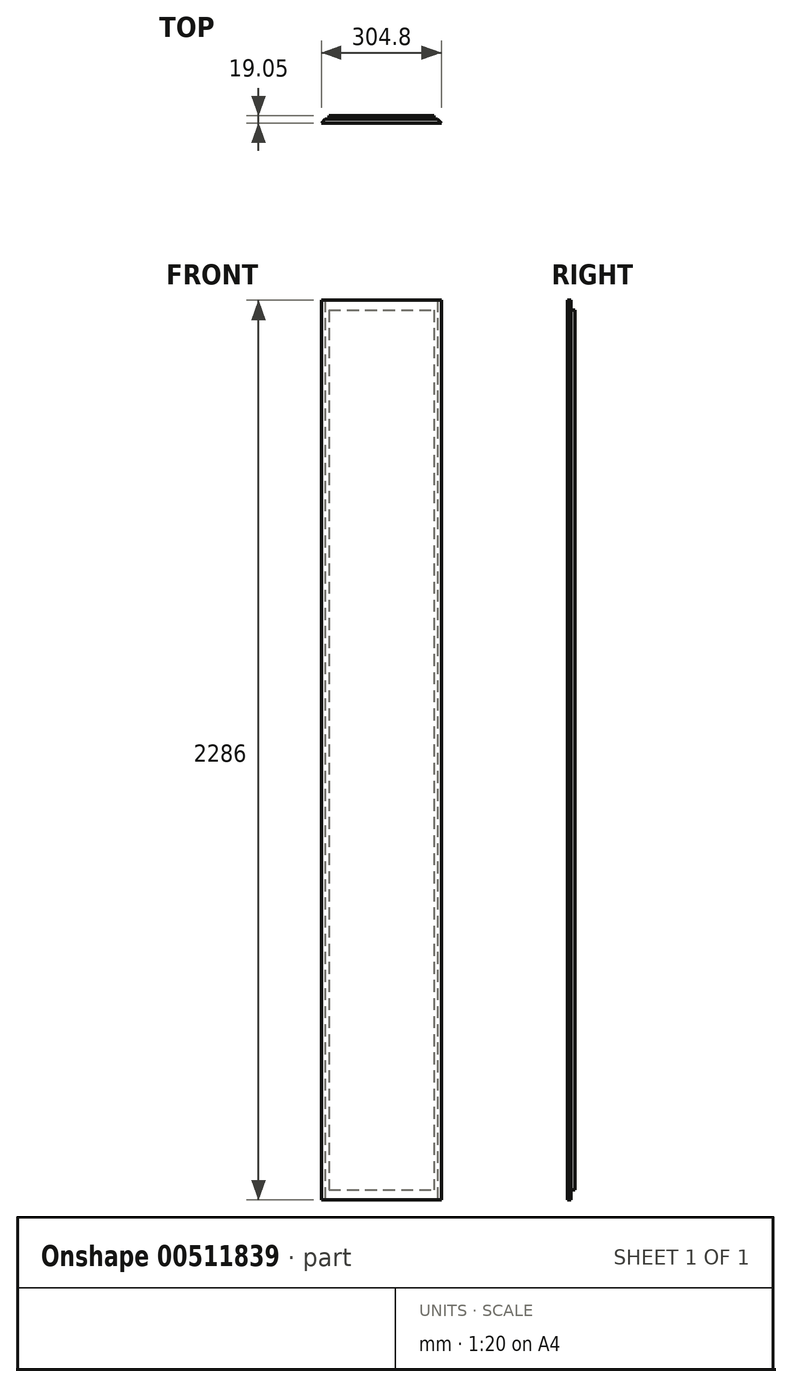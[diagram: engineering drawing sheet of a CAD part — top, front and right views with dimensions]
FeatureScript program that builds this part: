
annotation { "Feature Type Name" : "Feature", "Feature Type Description" : "" }
export const myFeature = defineFeature(function(context is Context, id is Id, definition is map)
    precondition{}
    {
        {
            var Q0;
            Q0=qCreatedBy(makeId("Top.planeOp"),FACE);
            var sketch = newSketch(context, id + "F0", { "sketchPlane" : qUnion([Q0])});
            skLineSegment(sketch, "E0.bottom", {"start": v(-140.62, 15.92) * mm, "end": v(164.18, 15.92) * mm});
            skLineSegment(sketch, "E0.top", {"start": v(-140.62, -3.13) * mm, "end": v(164.18, -3.13) * mm});
            skLineSegment(sketch, "E0.left", {"start": v(-140.62, 15.92) * mm, "end": v(-140.62, -3.13) * mm});
            skLineSegment(sketch, "E0.right", {"start": v(164.18, 15.92) * mm, "end": v(164.18, -3.13) * mm});
            skLineSegment(sketch, "E1", {"start": v(-140.62, -3.13) * mm, "end": v(-131.1, 6.4) * mm});
            skPoint(sketch, "E1.endSnap0", {"position": v(-140.62, 6.4) * mm});
            skLineSegment(sketch, "E2", {"start": v(-131.1, 6.4) * mm, "end": v(-121.57, 6.4) * mm});
            skLineSegment(sketch, "E3", {"start": v(-121.57, 6.4) * mm, "end": v(-121.57, 15.92) * mm});
            skLineSegment(sketch, "E4", {"start": v(11.78, 15.92) * mm, "end": v(11.78, -3.13) * mm, "construction": true});
            skLineSegment(sketch, "E5.MirrorCS", {"start": v(145.13, 6.4) * mm, "end": v(145.13, 15.92) * mm});
            skLineSegment(sketch, "E6.MirrorCS", {"start": v(154.66, 6.4) * mm, "end": v(145.13, 6.4) * mm});
            skLineSegment(sketch, "E7.MirrorCS", {"start": v(164.18, -3.13) * mm, "end": v(154.66, 6.4) * mm});
            skLineSegment(sketch, "E8.MirrorCS", {"start": v(164.18, 15.92) * mm, "end": v(-140.62, 15.92) * mm});
            skLineSegment(sketch, "E9", {"start": v(-121.57, 6.4) * mm, "end": v(145.13, 6.4) * mm});
            skSolve(sketch);
        }
        {
            var Q0;
            {var subQ0=sQuery(id+"F0.wireOp",EDGE,"E3");Q0=makeQuery(id+"F0.imprint","IMPRINT",FACE,{"disambiguationData":[TD([[makeQuery(id+"F0.imprint","IMPRINT",EDGE,{"derivedFrom":subQ0}),-1.0]])]});}
            var Q1;
            Q1=makeQuery(id+"F0.imprint","IMPRINT",FACE,{"disambiguationData":[TD([[makeQuery(id+"F0.imprint","IMPRINT",EDGE,{"derivedFrom":sQuery(id+"F0.wireOp",EDGE,"E0.top")}),1.0]])]});
            extrude(context, id + "F1", {"entities" : qUnion([Q0, Q1]), "depth" : 2286 * mm, "offsetDistance" : 25.4 * mm});
        }
        {
            var Q0;
            {var subQ0=sQuery(id+"F0.wireOp",EDGE,"E3");Q0=makeQuery(id+"F0.imprint","IMPRINT",FACE,{"disambiguationData":[TD([[makeQuery(id+"F0.imprint","IMPRINT",EDGE,{"derivedFrom":subQ0}),-1.0]])]});}
            extrude(context, id + "F2", {"entities" : qUnion([Q0]), "operationType" : NewBodyOperationType.REMOVE, "depth" : 25.4 * mm, "offsetDistance" : 25.4 * mm});
        }
        {
            var Q0;
            Q0=makeQuery(id+"F1.opExtrude","CAP_FACE",FACE,{"disambiguationData":[OSD([sQuery(id+"F0.wireOp",EDGE,"E0.top"),sQuery(id+"F0.wireOp",EDGE,"E1"),sQuery(id+"F0.wireOp",EDGE,"E2"),sQuery(id+"F0.wireOp",EDGE,"E3"),sQuery(id+"F0.wireOp",EDGE,"E5.MirrorCS"),sQuery(id+"F0.wireOp",EDGE,"E6.MirrorCS"),sQuery(id+"F0.wireOp",EDGE,"E7.MirrorCS"),sQuery(id+"F0.wireOp",EDGE,"E8.MirrorCS")])],"isStart":false});
            var sketch = newSketch(context, id + "F3", { "sketchPlane" : qUnion([Q0])});
            skLineSegment(sketch, "E10", {"start": v(-121.57, 6.4) * mm, "end": v(-121.57, 15.92) * mm});
            skLineSegment(sketch, "E11", {"start": v(-121.57, 15.92) * mm, "end": v(145.13, 15.92) * mm});
            skLineSegment(sketch, "E12", {"start": v(145.13, 15.92) * mm, "end": v(145.13, 6.4) * mm});
            skLineSegment(sketch, "E13", {"start": v(145.13, 6.4) * mm, "end": v(-121.57, 6.4) * mm});
            skSolve(sketch);
        }
        {
            var Q0;
            Q0=makeQuery(id+"F3.imprint","IMPRINT",FACE,{"disambiguationData":[TD([[makeQuery(id+"F3.imprint","IMPRINT",EDGE,{"derivedFrom":sQuery(id+"F3.wireOp",EDGE,"E10")}),-1.0]])]});
            extrude(context, id + "F4", {"entities" : qUnion([Q0]), "operationType" : NewBodyOperationType.REMOVE, "oppositeDirection" : true, "depth" : 25.4 * mm, "offsetDistance" : 25.4 * mm});
        }
    });
